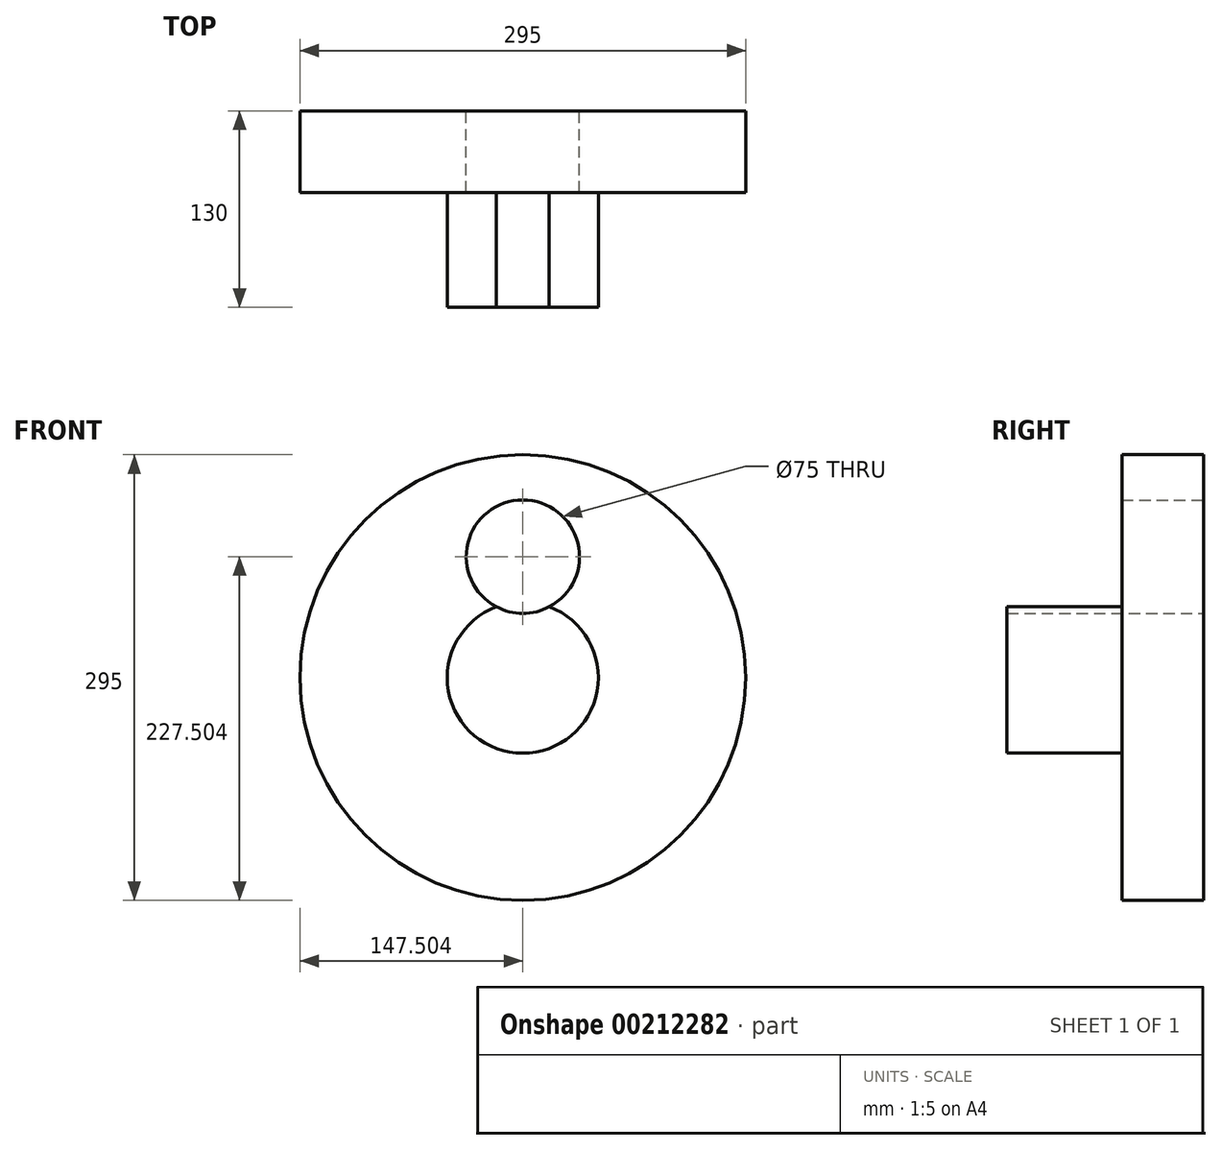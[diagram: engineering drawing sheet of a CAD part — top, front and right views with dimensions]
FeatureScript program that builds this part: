
annotation { "Feature Type Name" : "Feature", "Feature Type Description" : "" }
export const myFeature = defineFeature(function(context is Context, id is Id, definition is map)
    precondition{}
    {
        {
            var Q0;
            Q0=qCreatedBy(makeId("Front.planeOp"),FACE);
            var sketch = newSketch(context, id + "F0", { "sketchPlane" : qUnion([Q0])});
            skCircle(sketch, "E0", {"center": v(-82.28, -14.59) * mm, "radius": 147.5 * mm});
            skCircle(sketch, "E1", {"center": v(-82.28, -14.59) * mm, "radius": 50 * mm});
            skCircle(sketch, "E2", {"center": v(-82.28, 65.41) * mm, "radius": 37.5 * mm});
            skSolve(sketch);
        }
        {
            var Q0;
            Q0=makeQuery(id+"F0.imprint","IMPRINT",FACE,{"disambiguationData":[TD([[makeQuery(id+"F0.imprint","IMPRINT",EDGE,{"derivedFrom":sQuery(id+"F0.wireOp",EDGE,"E0")}),1.0]])]});
            var Q1;
            {var subQ0=sQuery(id+"F0.wireOp",EDGE,"E2");var subQ1=sQuery(id+"F0.wireOp",EDGE,"E1");var subQ2=makeQuery(id+"F0.imprint","INTERSECT",VERTEX,{"disambiguationData":[OD(0.0)],"derivedFrom":[subQ1,subQ0]});Q1=makeQuery(id+"F0.imprint","IMPRINT",FACE,{"disambiguationData":[TD([[makeQuery(id+"F0.imprint","IMPRINT",EDGE,{"disambiguationData":[TD([[subQ2,1.0]])],"derivedFrom":subQ1}),-1.0]])]});}
            var Q2;
            {var subQ0=sQuery(id+"F0.wireOp",EDGE,"E2");var subQ1=sQuery(id+"F0.wireOp",EDGE,"E1");var subQ2=makeQuery(id+"F0.imprint","INTERSECT",VERTEX,{"disambiguationData":[OD(0.0)],"derivedFrom":[subQ1,subQ0]});Q2=makeQuery(id+"F0.imprint","IMPRINT",FACE,{"disambiguationData":[TD([[makeQuery(id+"F0.imprint","IMPRINT",EDGE,{"disambiguationData":[TD([[subQ2,-1.0]])],"derivedFrom":subQ1}),1.0]])]});}
            var Q3;
            {var subQ0=sQuery(id+"F0.wireOp",EDGE,"E2");var subQ1=sQuery(id+"F0.wireOp",EDGE,"E1");var subQ2=makeQuery(id+"F0.imprint","INTERSECT",VERTEX,{"disambiguationData":[OD(0.0)],"derivedFrom":[subQ1,subQ0]});Q3=makeQuery(id+"F0.imprint","IMPRINT",FACE,{"disambiguationData":[TD([[makeQuery(id+"F0.imprint","IMPRINT",EDGE,{"disambiguationData":[TD([[subQ2,1.0]])],"derivedFrom":subQ1}),1.0]])]});}
            extrude(context, id + "F1", {"entities" : qUnion([Q0, Q1, Q2, Q3]), "depth" : 54 * mm});
        }
        {
            var Q0;
            {var subQ0=sQuery(id+"F0.wireOp",EDGE,"E2");var subQ1=sQuery(id+"F0.wireOp",EDGE,"E1");var subQ2=makeQuery(id+"F0.imprint","INTERSECT",VERTEX,{"disambiguationData":[OD(0.0)],"derivedFrom":[subQ1,subQ0]});Q0=makeQuery(id+"F0.imprint","IMPRINT",FACE,{"disambiguationData":[TD([[makeQuery(id+"F0.imprint","IMPRINT",EDGE,{"disambiguationData":[TD([[subQ2,1.0]])],"derivedFrom":subQ1}),-1.0]])]});}
            var Q1;
            {var subQ0=sQuery(id+"F0.wireOp",EDGE,"E2");var subQ1=sQuery(id+"F0.wireOp",EDGE,"E1");var subQ2=makeQuery(id+"F0.imprint","INTERSECT",VERTEX,{"disambiguationData":[OD(0.0)],"derivedFrom":[subQ1,subQ0]});Q1=makeQuery(id+"F0.imprint","IMPRINT",FACE,{"disambiguationData":[TD([[makeQuery(id+"F0.imprint","IMPRINT",EDGE,{"disambiguationData":[TD([[subQ2,1.0]])],"derivedFrom":subQ1}),1.0]])]});}
            extrude(context, id + "F2", {"entities" : qUnion([Q0, Q1]), "operationType" : NewBodyOperationType.REMOVE, "depth" : 54 * mm});
        }
        {
            var Q0;
            {var subQ0=sQuery(id+"F0.wireOp",EDGE,"E2");var subQ1=sQuery(id+"F0.wireOp",EDGE,"E1");var subQ2=makeQuery(id+"F0.imprint","INTERSECT",VERTEX,{"disambiguationData":[OD(0.0)],"derivedFrom":[subQ1,subQ0]});Q0=makeQuery(id+"F0.imprint","IMPRINT",FACE,{"disambiguationData":[TD([[makeQuery(id+"F0.imprint","IMPRINT",EDGE,{"disambiguationData":[TD([[subQ2,-1.0]])],"derivedFrom":subQ1}),1.0]])]});}
            var Q1;
            Q1=sQuery(id+"F0.wireOp",EDGE,"E1");
            extrude(context, id + "F3", {"entities" : qUnion([Q0]), "operationType" : NewBodyOperationType.ADD, "surfaceEntities" : qUnion([Q1]), "depth" : 130 * mm});
        }
    });
